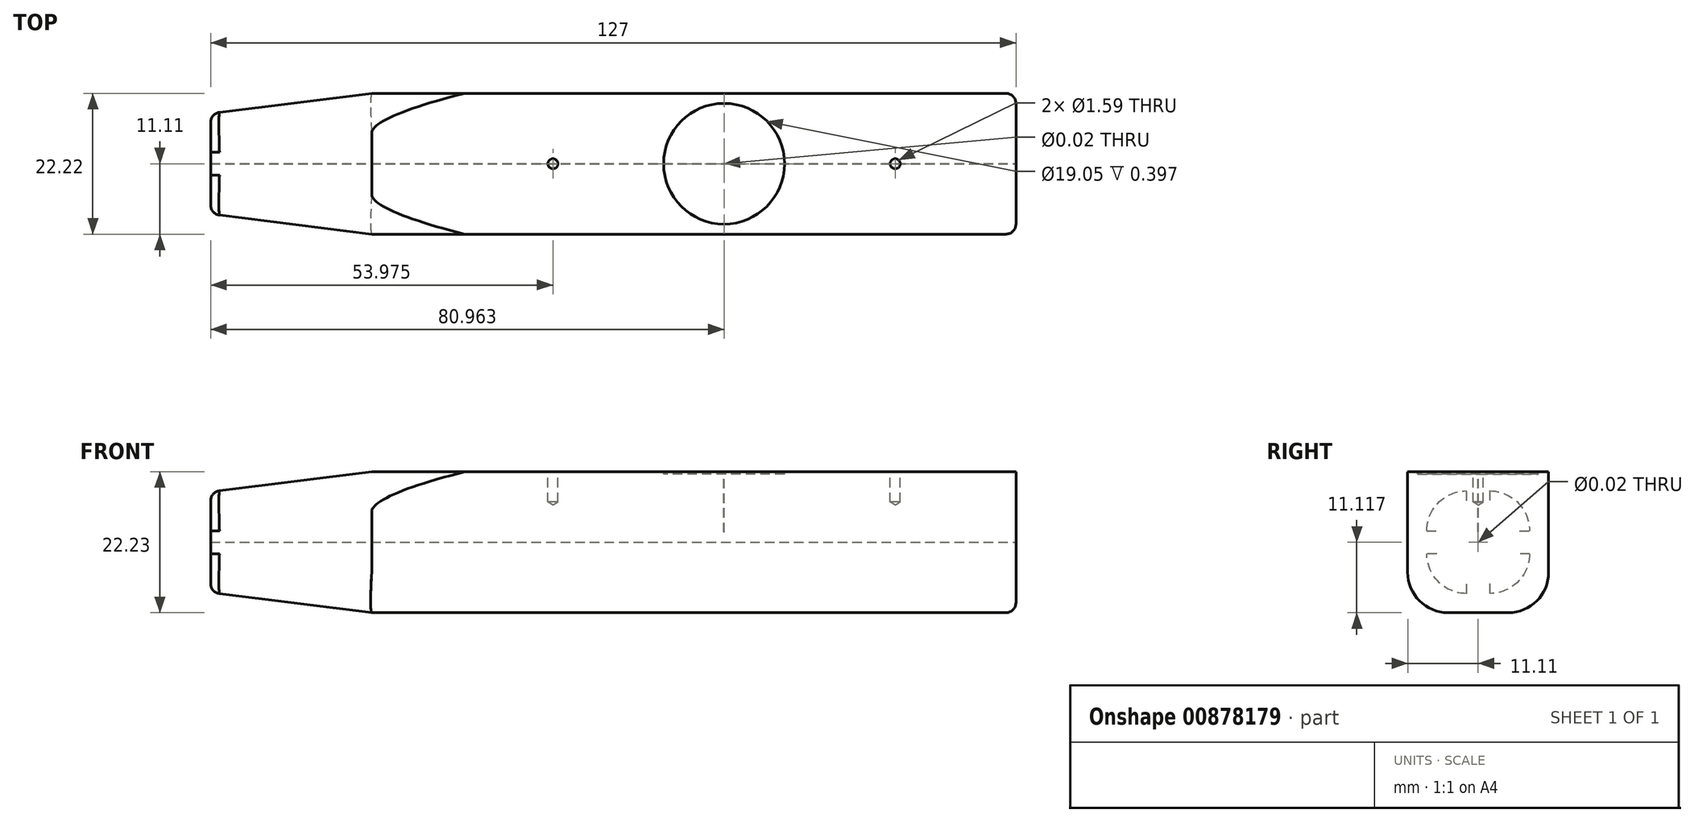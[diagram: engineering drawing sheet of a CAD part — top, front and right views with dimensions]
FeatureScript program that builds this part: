
annotation { "Feature Type Name" : "Feature", "Feature Type Description" : "" }
export const myFeature = defineFeature(function(context is Context, id is Id, definition is map)
    precondition{}
    {
        {
            var Q0;
            Q0=qCreatedBy(makeId("Top.planeOp"),FACE);
            var sketch = newSketch(context, id + "F0", { "sketchPlane" : qUnion([Q0])});
            skLineSegment(sketch, "E0.bottom", {"start": v(0, -11.11) * mm, "end": v(-127, -11.11) * mm});
            skLineSegment(sketch, "E0.top", {"start": v(0, 11.11) * mm, "end": v(-127, 11.11) * mm});
            skLineSegment(sketch, "E0.left", {"start": v(0, -11.11) * mm, "end": v(0, 11.11) * mm});
            skLineSegment(sketch, "E0.right", {"start": v(-127, -11.11) * mm, "end": v(-127, 11.11) * mm});
            skSolve(sketch);
        }
        {
            var Q0;
            Q0 = qSketchRegion(id + "F0", true);
            extrude(context, id + "F1", {"entities" : qUnion([Q0]), "oppositeDirection" : true, "depth" : 22.22 * mm, "offsetDistance" : 25.4 * mm});
        }
        {
            var Q0;
            Q0=qCreatedBy(makeId("Right.planeOp"),FACE);
            var sketch = newSketch(context, id + "F2", { "sketchPlane" : qUnion([Q0])});
            skCircle(sketch, "E1", {"center": v(0, -11.11) * mm, "radius": 4.96 * mm});
            skSolve(sketch);
        }
        {
            var Q0;
            Q0=qCreatedBy(makeId("Top.planeOp"),FACE);
            var sketch = newSketch(context, id + "F3", { "sketchPlane" : qUnion([Q0])});
            skCircle(sketch, "E2", {"center": v(-46.04, 0) * mm, "radius": 9.53 * mm});
            skCircle(sketch, "E3", {"center": v(-19.05, 0) * mm, "radius": 0.8 * mm});
            skCircle(sketch, "E4.MirrorC", {"center": v(-73.03, 0) * mm, "radius": 0.8 * mm});
            skSolve(sketch);
        }
        {
            var Q0;
            Q0=sQuery(id+"F3.wireOp",VERTEX,"E2.center");
            var Q1;
            Q1=makeQuery(id+"F1.opExtrude","SWEPT_BODY",BODY,{"disambiguationData":[OSD([sQuery(id+"F0.wireOp",EDGE,"E0.bottom"),sQuery(id+"F0.wireOp",EDGE,"E0.top"),sQuery(id+"F0.wireOp",EDGE,"E0.left"),sQuery(id+"F0.wireOp",EDGE,"E0.right")])]});
            hole(context, id + "F4", {"style" : HoleStyle.C_BORE, "endStyle" : HoleEndStyle.BLIND, "holeDiameter" : 9 / 406.4 * mm, "cBoreDiameter" : 19.05 * mm, "cBoreDepth" : 0.4 * mm, "majorDiameter" : 6.35 * mm, "holeDepth" : 9.52 * mm, "isTappedThrough" : true, "tappedDepth" : 12.7 * mm, "tapClearance" : 3, "startFromSketch" : true, "locations" : qUnion([Q0]), "scope" : qUnion([Q1])});
        }
        {
            var Q0;
            Q0=sQuery(id+"F2.wireOp",VERTEX,"E1.center");
            var Q1;
            Q1=makeQuery(id+"F1.opExtrude","SWEPT_BODY",BODY,{"disambiguationData":[OSD([sQuery(id+"F0.wireOp",EDGE,"E0.bottom"),sQuery(id+"F0.wireOp",EDGE,"E0.top"),sQuery(id+"F0.wireOp",EDGE,"E0.left"),sQuery(id+"F0.wireOp",EDGE,"E0.right")])]});
            hole(context, id + "F5", {"style" : HoleStyle.SIMPLE, "endStyle" : HoleEndStyle.THROUGH, "holeDiameter" : 25 / 1625.6 * mm, "majorDiameter" : 6.35 * mm, "isTappedThrough" : true, "tappedDepth" : 12.7 * mm, "tapClearance" : 3, "startFromSketch" : true, "locations" : qUnion([Q0]), "scope" : qUnion([Q1])});
        }
        {
            var Q0;
            Q0=sQuery(id+"F3.wireOp",VERTEX,"E3.center");
            var Q1;
            Q1=sQuery(id+"F3.wireOp",VERTEX,"E4.MirrorC.center");
            var Q2;
            Q2=makeQuery(id+"F1.opExtrude","SWEPT_BODY",BODY,{"disambiguationData":[OSD([sQuery(id+"F0.wireOp",EDGE,"E0.bottom"),sQuery(id+"F0.wireOp",EDGE,"E0.top"),sQuery(id+"F0.wireOp",EDGE,"E0.left"),sQuery(id+"F0.wireOp",EDGE,"E0.right")])]});
            hole(context, id + "F6", {"style" : HoleStyle.SIMPLE, "endStyle" : HoleEndStyle.BLIND, "holeDiameter" : 1.59 * mm, "majorDiameter" : 6.35 * mm, "holeDepth" : 4.76 * mm, "isTappedThrough" : true, "tappedDepth" : 12.7 * mm, "tapClearance" : 3, "startFromSketch" : true, "locations" : qUnion([Q0, Q1]), "scope" : qUnion([Q2])});
        }
        {
            var Q0;
            Q0=makeQuery(id+"F1.opExtrude","CAP_EDGE",EDGE,{"disambiguationData":[OSD([sQuery(id+"F0.wireOp",EDGE,"E0.right")])],"isStart":true});
            var Q1;
            Q1=makeQuery(id+"F1.opExtrude","SWEPT_EDGE",EDGE,{"disambiguationData":[OSD([sQuery(id+"F0.wireOp",EDGE,"E0.bottom"),sQuery(id+"F0.wireOp",EDGE,"E0.right")])]});
            var Q2;
            Q2=makeQuery(id+"F1.opExtrude","SWEPT_EDGE",EDGE,{"disambiguationData":[OSD([sQuery(id+"F0.wireOp",EDGE,"E0.top"),sQuery(id+"F0.wireOp",EDGE,"E0.right")])]});
            var Q3;
            Q3=makeQuery(id+"F1.opExtrude","CAP_EDGE",EDGE,{"disambiguationData":[OSD([sQuery(id+"F0.wireOp",EDGE,"E0.right")])],"isStart":false});
            chamfer(context, id + "F7", {"entities" : qUnion([Q0, Q1, Q2, Q3]), "chamferType" : ChamferType.TWO_OFFSETS, "width1" : 3.17 * mm, "oppositeDirection" : false, "width2" : 25.4 * mm, "tangentPropagation" : true});
        }
        {
            var Q0;
            {var subQ0=sQuery(id+"F0.wireOp",EDGE,"E0.right");Q0=makeQuery(id+"F7.opChamfer","BLEND_EDGE",EDGE,{"blendedFrom":[makeQuery(id+"F1.opExtrude","CAP_EDGE",EDGE,{"disambiguationData":[OSD([subQ0])],"isStart":true}),makeQuery(id+"F1.opExtrude","SWEPT_FACE",FACE,{"disambiguationData":[OSD([subQ0])]})],"blendedInto":[makeQuery(id+"F1.opExtrude","SWEPT_FACE",FACE,{"disambiguationData":[OSD([subQ0])]})]});}
            var Q1;
            {var subQ0=sQuery(id+"F0.wireOp",EDGE,"E0.right");Q1=makeQuery(id+"F7.opChamfer","BLEND_EDGE",EDGE,{"blendedFrom":[makeQuery(id+"F1.opExtrude","SWEPT_EDGE",EDGE,{"disambiguationData":[OSD([sQuery(id+"F0.wireOp",EDGE,"E0.bottom"),subQ0])]}),makeQuery(id+"F1.opExtrude","SWEPT_FACE",FACE,{"disambiguationData":[OSD([subQ0])]})],"blendedInto":[makeQuery(id+"F1.opExtrude","SWEPT_FACE",FACE,{"disambiguationData":[OSD([subQ0])]})]});}
            var Q2;
            {var subQ0=sQuery(id+"F0.wireOp",EDGE,"E0.right");Q2=makeQuery(id+"F7.opChamfer","BLEND_EDGE",EDGE,{"blendedFrom":[makeQuery(id+"F1.opExtrude","CAP_EDGE",EDGE,{"disambiguationData":[OSD([subQ0])],"isStart":false}),makeQuery(id+"F1.opExtrude","SWEPT_FACE",FACE,{"disambiguationData":[OSD([subQ0])]})],"blendedInto":[makeQuery(id+"F1.opExtrude","SWEPT_FACE",FACE,{"disambiguationData":[OSD([subQ0])]})]});}
            var Q3;
            {var subQ0=sQuery(id+"F0.wireOp",EDGE,"E0.right");Q3=makeQuery(id+"F7.opChamfer","BLEND_EDGE",EDGE,{"blendedFrom":[makeQuery(id+"F1.opExtrude","SWEPT_EDGE",EDGE,{"disambiguationData":[OSD([sQuery(id+"F0.wireOp",EDGE,"E0.top"),subQ0])]}),makeQuery(id+"F1.opExtrude","SWEPT_FACE",FACE,{"disambiguationData":[OSD([subQ0])]})],"blendedInto":[makeQuery(id+"F1.opExtrude","SWEPT_FACE",FACE,{"disambiguationData":[OSD([subQ0])]})]});}
            var Q4;
            Q4=makeQuery(id+"F1.opExtrude","SWEPT_EDGE",EDGE,{"disambiguationData":[OSD([sQuery(id+"F0.wireOp",EDGE,"E0.bottom"),sQuery(id+"F0.wireOp",EDGE,"E0.left")])]});
            var Q5;
            Q5=makeQuery(id+"F1.opExtrude","CAP_EDGE",EDGE,{"disambiguationData":[OSD([sQuery(id+"F0.wireOp",EDGE,"E0.left")])],"isStart":false});
            var Q6;
            Q6=makeQuery(id+"F1.opExtrude","SWEPT_EDGE",EDGE,{"disambiguationData":[OSD([sQuery(id+"F0.wireOp",EDGE,"E0.top"),sQuery(id+"F0.wireOp",EDGE,"E0.left")])]});
            fillet(context, id + "F8", {"entities" : qUnion([Q0, Q1, Q2, Q3, Q4, Q5, Q6]), "radius" : 1.59 * mm, "tangentPropagation" : true, "allowEdgeOverflow" : false});
        }
        {
            var Q0;
            {var subQ0=sQuery(id+"F0.wireOp",EDGE,"E0.right");Q0=makeQuery(id+"F7.opChamfer","BLEND_EDGE",EDGE,{"blendedFrom":[makeQuery(id+"F1.opExtrude","SWEPT_EDGE",EDGE,{"disambiguationData":[OSD([sQuery(id+"F0.wireOp",EDGE,"E0.top"),subQ0])]}),makeQuery(id+"F1.opExtrude","CAP_EDGE",EDGE,{"disambiguationData":[OSD([subQ0])],"isStart":true})],"blendedInto":[]});}
            var Q1;
            {var subQ0=sQuery(id+"F0.wireOp",EDGE,"E0.right");Q1=makeQuery(id+"F7.opChamfer","BLEND_EDGE",EDGE,{"blendedFrom":[makeQuery(id+"F1.opExtrude","SWEPT_EDGE",EDGE,{"disambiguationData":[OSD([sQuery(id+"F0.wireOp",EDGE,"E0.bottom"),subQ0])]}),makeQuery(id+"F1.opExtrude","CAP_EDGE",EDGE,{"disambiguationData":[OSD([subQ0])],"isStart":true})],"blendedInto":[]});}
            var Q2;
            {var subQ0=sQuery(id+"F0.wireOp",EDGE,"E0.right");Q2=makeQuery(id+"F7.opChamfer","BLEND_EDGE",EDGE,{"blendedFrom":[makeQuery(id+"F1.opExtrude","SWEPT_EDGE",EDGE,{"disambiguationData":[OSD([sQuery(id+"F0.wireOp",EDGE,"E0.bottom"),subQ0])]}),makeQuery(id+"F1.opExtrude","CAP_EDGE",EDGE,{"disambiguationData":[OSD([subQ0])],"isStart":false})],"blendedInto":[]});}
            var Q3;
            {var subQ0=sQuery(id+"F0.wireOp",EDGE,"E0.right");Q3=makeQuery(id+"F7.opChamfer","BLEND_EDGE",EDGE,{"blendedFrom":[makeQuery(id+"F1.opExtrude","SWEPT_EDGE",EDGE,{"disambiguationData":[OSD([sQuery(id+"F0.wireOp",EDGE,"E0.top"),subQ0])]}),makeQuery(id+"F1.opExtrude","CAP_EDGE",EDGE,{"disambiguationData":[OSD([subQ0])],"isStart":false})],"blendedInto":[]});}
            var Q4;
            Q4=makeQuery(id+"F1.opExtrude","CAP_EDGE",EDGE,{"disambiguationData":[OSD([sQuery(id+"F0.wireOp",EDGE,"E0.bottom")])],"isStart":false});
            var Q5;
            Q5=makeQuery(id+"F1.opExtrude","CAP_EDGE",EDGE,{"disambiguationData":[OSD([sQuery(id+"F0.wireOp",EDGE,"E0.top")])],"isStart":false});
            fillet(context, id + "F9", {"entities" : qUnion([Q0, Q1, Q2, Q3, Q4, Q5]), "radius" : 6.35 * mm, "tangentPropagation" : true, "allowEdgeOverflow" : false});
        }
    });
